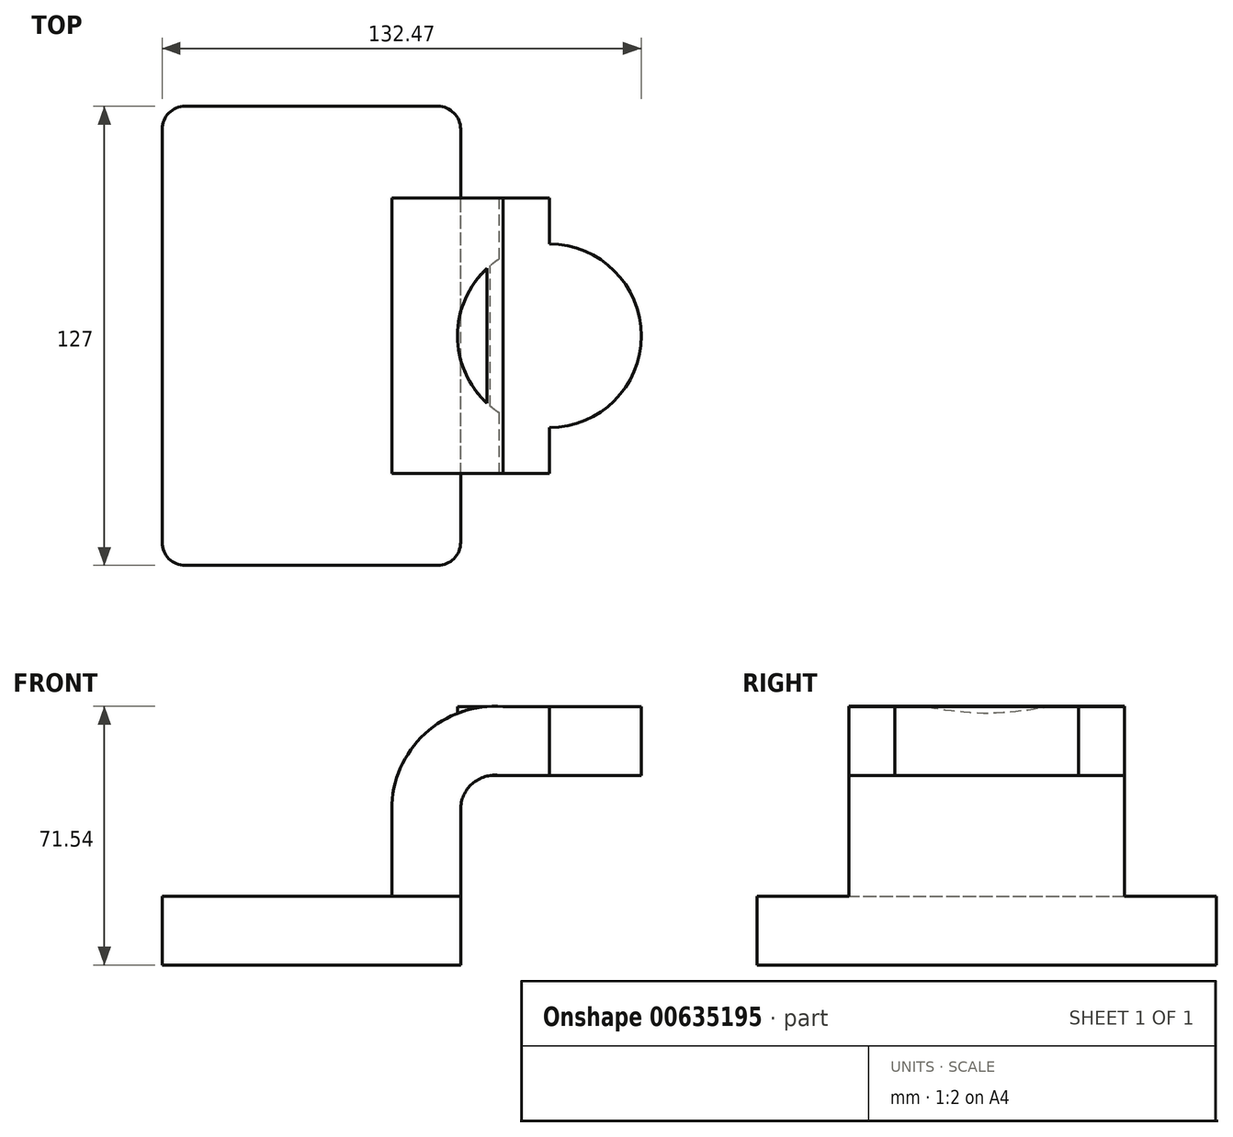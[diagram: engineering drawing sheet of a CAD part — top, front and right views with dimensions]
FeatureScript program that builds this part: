
annotation { "Feature Type Name" : "Feature", "Feature Type Description" : "" }
export const myFeature = defineFeature(function(context is Context, id is Id, definition is map)
    precondition{}
    {
        {
            var Q0;
            Q0=qCreatedBy(makeId("Front.planeOp"),FACE);
            var sketch = newSketch(context, id + "F0", { "sketchPlane" : qUnion([Q0])});
            skLineSegment(sketch, "E0.bottom", {"start": v(41.28, -9.52) * mm, "end": v(-41.28, -9.53) * mm});
            skLineSegment(sketch, "E0.top", {"start": v(41.28, 9.53) * mm, "end": v(-41.28, 9.53) * mm});
            skLineSegment(sketch, "E0.left", {"start": v(41.28, -9.52) * mm, "end": v(41.28, 9.53) * mm});
            skLineSegment(sketch, "E0.right", {"start": v(-41.28, -9.53) * mm, "end": v(-41.28, 9.53) * mm});
            skPoint(sketch, "E0.middle", {"position": v(0, 0) * mm});
            skLineSegment(sketch, "E1.bottom", {"start": v(116.6, 38.1) * mm, "end": v(65.8, 38.1) * mm});
            skLineSegment(sketch, "E1.top", {"start": v(116.6, 66.68) * mm, "end": v(65.8, 66.68) * mm});
            skLineSegment(sketch, "E1.left", {"start": v(116.6, 38.1) * mm, "end": v(116.6, 66.68) * mm});
            skLineSegment(sketch, "E1.right", {"start": v(65.8, 38.1) * mm, "end": v(65.8, 66.68) * mm});
            skPoint(sketch, "E1.middle", {"position": v(91.2, 52.39) * mm});
            skLineSegment(sketch, "E2", {"start": v(41.28, 9.53) * mm, "end": v(41.28, 33.48) * mm});
            skArc(sketch, "E3", {"start": v(41.27, 33.48) * mm, "mid": v(44.52, 40.62) * mm, "end": v(52.03, 42.88) * mm});
            skLineSegment(sketch, "E4", {"start": v(52.03, 42.88) * mm, "end": v(91.2, 42.88) * mm});
            skLineSegment(sketch, "E5.0", {"start": v(52.96, 61.93) * mm, "end": v(91.2, 61.93) * mm});
            skArc(sketch, "E5.1", {"start": v(22.22, 33.48) * mm, "mid": v(31.38, 54.42) * mm, "end": v(52.96, 61.93) * mm});
            skLineSegment(sketch, "E5.2", {"start": v(22.22, 9.53) * mm, "end": v(22.22, 33.48) * mm});
            skLineSegment(sketch, "E6", {"start": v(91.2, 66.68) * mm, "end": v(91.2, 38.1) * mm});
            skFitSpline(sketch, "E7", {"points": [v(-41.28, 9.53) * mm, v(65.8, 66.68) * mm], "startDerivative": vector(23.47, 110.78) * mm, "endDerivative": vector(185.1, -6.62) * mm});
            skSolve(sketch);
        }
        {
            var Q0;
            Q0=makeQuery(id+"F0.imprint","IMPRINT",FACE,{"disambiguationData":[TD([[makeQuery(id+"F0.imprint","IMPRINT",EDGE,{"derivedFrom":sQuery(id+"F0.wireOp",EDGE,"E0.bottom")}),-1.0]])]});
            extrude(context, id + "F1", {"entities" : qUnion([Q0]), "endBound" : BoundingType.SYMMETRIC, "depth" : 127 * mm});
        }
        {
            var Q0;
            {var subQ1=sQuery(id+"F0.wireOp",EDGE,"E2");Q0=makeQuery(id+"F0.imprint","IMPRINT",FACE,{"disambiguationData":[TD([[makeQuery(id+"F0.imprint","IMPRINT",EDGE,{"derivedFrom":subQ1}),1.0]])]});}
            extrude(context, id + "F2", {"entities" : qUnion([Q0]), "operationType" : NewBodyOperationType.ADD, "endBound" : BoundingType.SYMMETRIC, "depth" : 76.2 * mm});
        }
        {
            var Q0;
            {var subQ0=sQuery(id+"F0.wireOp",EDGE,"E5.1");Q0=makeQuery(id+"F0.imprint","IMPRINT",FACE,{"disambiguationData":[TD([[makeQuery(id+"F0.imprint","IMPRINT",EDGE,{"derivedFrom":subQ0}),1.0]])]});}
            extrude(context, id + "F3", {"entities" : qUnion([Q0]), "operationType" : NewBodyOperationType.ADD, "endBound" : BoundingType.SYMMETRIC, "depth" : 15.88 * mm});
        }
        {
            var Q0;
            {var subQ0=sQuery(id+"F0.wireOp",EDGE,"E4");var subQ1=sQuery(id+"F0.wireOp",EDGE,"E1.right");var subQ2=makeQuery(id+"F0.imprint","INTERSECT",VERTEX,{"derivedFrom":[subQ1,subQ0]});Q0=makeQuery(id+"F0.imprint","IMPRINT",FACE,{"disambiguationData":[TD([[makeQuery(id+"F0.imprint","IMPRINT",EDGE,{"disambiguationData":[TD([[subQ2,-1.0]])],"derivedFrom":subQ1}),-1.0]])]});}
            var Q1;
            Q1=sQuery(id+"F0.wireOp",EDGE,"E1.right");
            revolve(context, id + "F4", {"operationType" : NewBodyOperationType.ADD, "entities" : qUnion([Q0]), "axis" : qUnion([Q1]), "revolveType" : RevolveType.FULL});
        }
        {
            var Q0;
            Q0=makeQuery(id+"F1.opExtrude","CAP_EDGE",EDGE,{"disambiguationData":[OSD([sQuery(id+"F0.wireOp",EDGE,"E0.left")])],"isStart":false});
            var Q1;
            Q1=makeQuery(id+"F1.opExtrude","CAP_EDGE",EDGE,{"disambiguationData":[OSD([sQuery(id+"F0.wireOp",EDGE,"E0.left")])],"isStart":true});
            var Q2;
            Q2=makeQuery(id+"F1.opExtrude","CAP_EDGE",EDGE,{"disambiguationData":[OSD([sQuery(id+"F0.wireOp",EDGE,"E0.right")])],"isStart":true});
            var Q3;
            Q3=makeQuery(id+"F1.opExtrude","CAP_EDGE",EDGE,{"disambiguationData":[OSD([sQuery(id+"F0.wireOp",EDGE,"E0.right")])],"isStart":false});
            fillet(context, id + "F5", {"entities" : qUnion([Q0, Q1, Q2, Q3]), "radius" : 6.35 * mm, "tangentPropagation" : true, "allowEdgeOverflow" : false});
        }
    });
